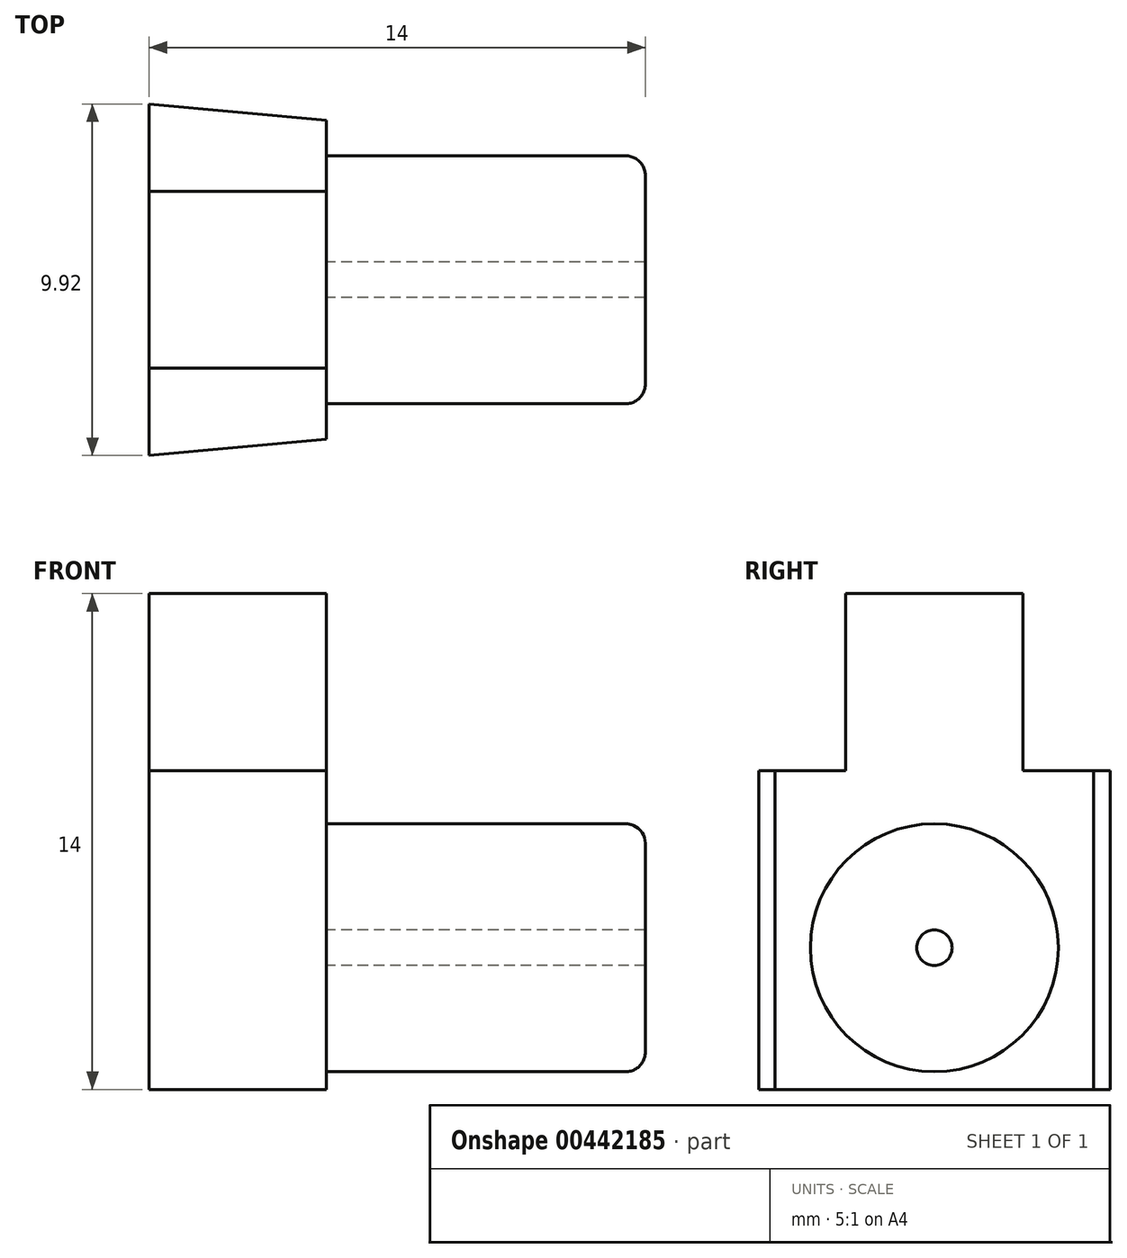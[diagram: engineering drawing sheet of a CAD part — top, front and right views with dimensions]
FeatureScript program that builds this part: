
annotation { "Feature Type Name" : "Feature", "Feature Type Description" : "" }
export const myFeature = defineFeature(function(context is Context, id is Id, definition is map)
    precondition{}
    {
        {
            var Q0;
            Q0=qCreatedBy(makeId("Top.planeOp"),FACE);
            var sketch = newSketch(context, id + "F0", { "sketchPlane" : qUnion([Q0])});
            skLineSegment(sketch, "E0.bottom", {"start": v(2.5, 2.5) * mm, "end": v(-2.5, 2.5) * mm});
            skLineSegment(sketch, "E0.top", {"start": v(2.5, -2.5) * mm, "end": v(-2.5, -2.5) * mm});
            skLineSegment(sketch, "E0.left", {"start": v(2.5, 2.5) * mm, "end": v(2.5, -2.5) * mm});
            skPoint(sketch, "E0.middle", {"position": v(0, 0) * mm});
            skLineSegment(sketch, "E1.left", {"start": v(2.5, 4.5) * mm, "end": v(2.5, -4.5) * mm});
            skLineSegment(sketch, "E2", {"start": v(2.5, 4.5) * mm, "end": v(-2.5, 4.96) * mm});
            skLineSegment(sketch, "E3", {"start": v(2.5, -4.5) * mm, "end": v(-2.5, -4.96) * mm});
            skLineSegment(sketch, "E4", {"start": v(-2.5, 4.96) * mm, "end": v(-2.5, -4.96) * mm});
            skLineSegment(sketch, "E5", {"start": v(2.5, 4.5) * mm, "end": v(-0.24, 4.5) * mm, "construction": true});
            skLineSegment(sketch, "E6", {"start": v(2.5, -4.5) * mm, "end": v(-1.22, -4.5) * mm, "construction": true});
            skLineSegment(sketch, "E7", {"start": v(-3.03, 0) * mm, "end": v(2.5, 0) * mm, "construction": true});
            skPoint(sketch, "E7.startSnap0", {"position": v(2.5, 0) * mm});
            skSolve(sketch);
        }
        {
            var Q0;
            {var subQ0=sQuery(id+"F0.wireOp",EDGE,"E0.bottom");Q0=makeQuery(id+"F0.imprint","IMPRINT",FACE,{"disambiguationData":[TD([[makeQuery(id+"F0.imprint","IMPRINT",EDGE,{"derivedFrom":subQ0}),1.0]])]});}
            extrude(context, id + "F1", {"entities" : qUnion([Q0]), "depth" : 14 * mm});
        }
        {
            var Q0;
            {var subQ0=sQuery(id+"F0.wireOp",EDGE,"E0.bottom");Q0=makeQuery(id+"F0.imprint","IMPRINT",FACE,{"disambiguationData":[TD([[makeQuery(id+"F0.imprint","IMPRINT",EDGE,{"derivedFrom":subQ0}),-1.0]])]});}
            var Q1;
            {var subQ0=sQuery(id+"F0.wireOp",EDGE,"E0.top");Q1=makeQuery(id+"F0.imprint","IMPRINT",FACE,{"disambiguationData":[TD([[makeQuery(id+"F0.imprint","IMPRINT",EDGE,{"derivedFrom":subQ0}),1.0]])]});}
            extrude(context, id + "F2", {"entities" : qUnion([Q0, Q1]), "operationType" : NewBodyOperationType.ADD, "depth" : 9 * mm});
        }
        {
            var Q0;
            {var subQ0=sQuery(id+"F0.wireOp",EDGE,"E1.left");Q0=makeQuery(id+"F2.boolean.opBoolean","MERGE",FACE,{"derivedFrom":[makeQuery(id+"F1.opExtrude","SWEPT_FACE",FACE,{"disambiguationData":[OSD([subQ0])]}),makeQuery(id+"F2.opExtrude","SWEPT_FACE",FACE,{"disambiguationData":[OSD([subQ0]),TDD([makeQuery(id+"F0.imprint","IMPRINT",EDGE,{"disambiguationData":[TD([[makeQuery(id+"F0.imprint","INTERSECT",VERTEX,{"derivedFrom":[sQuery(id+"F0.wireOp",EDGE,"E0.bottom"),subQ0]}),1.0]])],"derivedFrom":subQ0})])]}),makeQuery(id+"F2.opExtrude","SWEPT_FACE",FACE,{"disambiguationData":[OSD([subQ0]),TDD([makeQuery(id+"F0.imprint","IMPRINT",EDGE,{"disambiguationData":[TD([[makeQuery(id+"F0.imprint","INTERSECT",VERTEX,{"derivedFrom":[sQuery(id+"F0.wireOp",EDGE,"E0.top"),subQ0]}),-1.0]])],"derivedFrom":subQ0})])]})]});}
            var sketch = newSketch(context, id + "F3", { "sketchPlane" : qUnion([Q0])});
            skLineSegment(sketch, "E8", {"start": v(0, 14) * mm, "end": v(0, 0) * mm, "construction": true});
            skLineSegment(sketch, "E9", {"start": v(4.5, 9) * mm, "end": v(4.5, 9) * mm});
            skCircle(sketch, "E10", {"center": v(0, 4) * mm, "radius": 3.5 * mm});
            skCircle(sketch, "E11", {"center": v(0, 4) * mm, "radius": 0.5 * mm});
            skSolve(sketch);
        }
        {
            var Q0;
            Q0=makeQuery(id+"F3.imprint","IMPRINT",FACE,{"disambiguationData":[TD([[makeQuery(id+"F3.imprint","IMPRINT",EDGE,{"derivedFrom":sQuery(id+"F3.wireOp",EDGE,"E10")}),1.0]])]});
            extrude(context, id + "F4", {"entities" : qUnion([Q0]), "operationType" : NewBodyOperationType.ADD, "depth" : 9 * mm});
        }
        {
            var Q0;
            Q0=makeQuery(id+"F4.opExtrude","CAP_EDGE",EDGE,{"disambiguationData":[OSD([sQuery(id+"F3.wireOp",EDGE,"E10")])],"isStart":true});
            var Q1;
            Q1=makeQuery(id+"F4.opExtrude","CAP_EDGE",EDGE,{"disambiguationData":[OSD([sQuery(id+"F3.wireOp",EDGE,"E10")])],"isStart":false});
            fillet(context, id + "F5", {"entities" : qUnion([Q0, Q1]), "radius" : .55 * mm, "tangentPropagation" : true, "allowEdgeOverflow" : false});
        }
    });
